FCSTD DOCUMENT  (FreeCAD 2024.2R37179 (Git))
Label: Assembly
License: All rights reserved
LicenseURL: https://en.wikipedia.org/wiki/All_rights_reserved
objects: App::Link×2, Assembly::JointGroup×1, Assembly::AssemblyObject×1
EXTERNAL_REF file=Base.FCStd obj=Body
EXTERNAL_REF file=22mm.FCStd obj=Body

FEATURE [Assembly::JointGroup] Joints
FEATURE [App::Link] Body
  LinkPlacement = pos=(38.752,-106.986,43.991) rot=(0,0,1;0rad)
  LinkedObject = -> <external Base.FCStd>#Body
  Placement = pos=(38.752,-106.986,43.991) rot=(0,0,1;0rad)
FEATURE [App::Link] Body001
  LinkPlacement = pos=(28.252,-67.4863,52.991) rot=(0,0,1;1.5708rad)
  LinkedObject = -> <external 22mm.FCStd>#Body
  Placement = pos=(28.252,-67.4863,52.991) rot=(0,0,1;1.5708rad)
FEATURE [Assembly::AssemblyObject] Assembly
  Group = -> [Joints,Body,Body001]
  Origin = -> Origin
  Type = Assembly

RESOLVED EXTERNAL PARTS (link-assembly join: the EXTERNAL_REF files above that resolve inside this repo's crawl, each included once):
---- part 22mm.FCStd = doc fcstd_51c7ecd0057d ----
FCSTD DOCUMENT  (FreeCAD 2024.2R37179 (Git))
Label: 22mm
License: All rights reserved
LicenseURL: https://en.wikipedia.org/wiki/All_rights_reserved
objects: Sketcher::SketchObject×1, PartDesign::Pad×1, PartDesign::Fillet×1, PartDesign::Body×1
note: 6 computed .brp shape members not serialized (recipe doc carries the construction recipe); baked Part::Feature solids carry a one-line shape summary decoded from their .brp

FEATURE [Sketcher::SketchObject] Sketch
  AttachmentSupport = -> [XZ_Plane]
  FullyConstrained = true
  MapMode = 5
  Placement = pos=(0,0,0) rot=(1,0,0;1.5708rad)
  sketch-geometry (4):
    g0: LineSegment StartX=0 StartY=0 StartZ=0 EndX=0 EndY=22 EndZ=0
    g1: LineSegment StartX=0 StartY=22 StartZ=0 EndX=80 EndY=10 EndZ=0
    g2: LineSegment StartX=80 StartY=10 StartZ=0 EndX=80 EndY=0 EndZ=0
    g3: LineSegment StartX=80 StartY=0 StartZ=0 EndX=0 EndY=0 EndZ=0
  constraints (11):
    c: Coincident(g-1,g0)
    c: PointOnObject(g0,g-2)
    c: Coincident(g0,g1)
    c: Coincident(g1,g2)
    c: PointOnObject(g2,g-1)
    c: Vertical(g2)
    c: Coincident(g2,g3)
    c: Coincident(g3,g0)
    c: DistanceY(g0,g0) = 22
    c: DistanceY(g2,g2) = 10
    c: DistanceX(g3,g3) = 80
FEATURE [PartDesign::Pad] Pad
  Direction = (0,-1,2e-16)
  Length = 20
  Length2 = 10
  Placement = pos=(0,0,0) rot=(1,0,0;1.5708rad)
  Profile = -> Sketch
  ReferenceAxis = -> Sketch [N_Axis]
  Refine = true
  Suppressed = false
  Type = 0
FEATURE [PartDesign::Fillet] Fillet
  Base = -> Pad [Edge6]
  BaseFeature = -> Pad
  Placement = pos=(0,0,0) rot=(1,0,0;1.5708rad)
  Radius = 2
  Refine = true
  SupportTransform = false
  Suppressed = false
  UseAllEdges = true
FEATURE [PartDesign::Body] Body
  Group = -> [Sketch,Pad,Fillet]
  Origin = -> Origin
  Tip = -> Fillet
---- part Base.FCStd = doc fcstd_2ecf710a8f8c ----
FCSTD DOCUMENT  (FreeCAD 2024.2R37179 (Git))
Label: Base
License: All rights reserved
LicenseURL: https://en.wikipedia.org/wiki/All_rights_reserved
objects: PartDesign::Fillet×5, Sketcher::SketchObject×2, PartDesign::Pad×2, PartDesign::LinearPattern×2, PartDesign::MultiTransform×1, PartDesign::Body×1
note: 20 computed .brp shape members not serialized (recipe doc carries the construction recipe); baked Part::Feature solids carry a one-line shape summary decoded from their .brp

FEATURE [Sketcher::SketchObject] Sketch
  AttachmentSupport = -> [XY_Plane]
  FullyConstrained = true
  MapMode = 5
  sketch-geometry (10):
    g0: LineSegment StartX=-37.5 StartY=-37.5 StartZ=0 EndX=37.5 EndY=-37.5 EndZ=0
    g1: LineSegment StartX=37.5 StartY=-37.5 StartZ=0 EndX=37.5 EndY=37.5 EndZ=0
    g2: LineSegment StartX=37.5 StartY=37.5 StartZ=0 EndX=10 EndY=37.5 EndZ=0
    g3: LineSegment StartX=-37.5 StartY=37.5 StartZ=0 EndX=-37.5 EndY=-37.5 EndZ=0
    g4: GeomPoint X=0 Y=0 Z=0
    g5: LineSegment StartX=-10 StartY=117.5 StartZ=0 EndX=-10 EndY=37.5 EndZ=0
    g6: LineSegment StartX=10 StartY=37.5 StartZ=0 EndX=10 EndY=117.5 EndZ=0
    g7: LineSegment StartX=10 StartY=117.5 StartZ=0 EndX=-10 EndY=117.5 EndZ=0
    g8: GeomPoint X=0 Y=77.5 Z=0
    g9: LineSegment StartX=-10 StartY=37.5 StartZ=0 EndX=-37.5 EndY=37.5 EndZ=0
  constraints (25):
    c: Coincident(g0,g1)
    c: Coincident(g1,g2)
    c: Coincident(g9,g3)
    c: Coincident(g3,g0)
    c: Horizontal(g0)
    c: Horizontal(g2)
    c: Vertical(g1)
    c: Vertical(g3)
    c: Symmetric(g2,g0,g4)
    c: Distance(g1,g3) = 75
    c: Distance(g0,g9) = 75
    c: Coincident(g4,g-1)
    c: Coincident(g6,g7)
    c: Coincident(g7,g5)
    c: Vertical(g5)
    c: Vertical(g6)
    c: Horizontal(g7)
    c: Symmetric(g6,g5,g8)
    c: PointOnObject(g8,g-2)
    c: Distance(g7,g7) = 20
    c: DistanceY(g6,g6) = 80
    c: Horizontal(g9)
    c: Coincident(g5,g9)
    c: Coincident(g6,g2)
    c: Horizontal(g5,g2)
FEATURE [PartDesign::Pad] Pad
  Direction = (0,0,1)
  Length = 3
  Length2 = 10
  Profile = -> Sketch
  ReferenceAxis = -> Sketch [N_Axis]
  Refine = true
  Suppressed = false
  Type = 0
FEATURE [PartDesign::Fillet] Fillet
  Base = -> Pad [Edge5,Edge2,Edge20,Edge1]
  BaseFeature = -> Pad
  Radius = 5
  Refine = true
  SupportTransform = false
  Suppressed = false
  UseAllEdges = false
FEATURE [Sketcher::SketchObject] Sketch001
  AttachmentSupport = -> [Fillet]
  FullyConstrained = true
  MapMode = 5
  Placement = pos=(0,0,3) rot=(0,0,1;0rad)
  sketch-geometry (1):
    g0: Circle CenterX=-30 CenterY=30 CenterZ=0 NormalX=0 NormalY=0 NormalZ=1 AngleXU=0 Radius=2.5
  constraints (3):
    c: Diameter(g0) = 5
    c: DistanceX(g0,g-1) = 30
    c: DistanceY(g-1,g0) = 30
FEATURE [PartDesign::Pad] Pad001
  BaseFeature = -> Fillet
  Direction = (0,0,1)
  Length = 1.5
  Length2 = 10
  Profile = -> Sketch001
  ReferenceAxis = -> Sketch001 [N_Axis]
  Refine = true
  Suppressed = false
  Type = 0
FEATURE [PartDesign::LinearPattern] LinearPattern
  Direction = -> X_Axis
  Length = 60
  Mode = 0
  Occurrences = 5
  Offset = 15
  Refine = true
  Suppressed = false
FEATURE [PartDesign::LinearPattern] LinearPattern001
  Direction = -> Y_Axis
  Length = 60
  Mode = 0
  Occurrences = 4
  Offset = 20
  Refine = true
  Reversed = true
  Suppressed = false
FEATURE [PartDesign::MultiTransform] MultiTransform
  BaseFeature = -> Pad001
  Originals = -> [Pad001]
  Refine = true
  Suppressed = false
  Transformations = -> [LinearPattern,LinearPattern001]
FEATURE [PartDesign::Fillet] Fillet001
  Base = -> MultiTransform [Edge4]
  BaseFeature = -> MultiTransform
  Radius = 1
  Refine = true
  SupportTransform = false
  Suppressed = false
  UseAllEdges = false
FEATURE [PartDesign::Fillet] Fillet002
  Base = -> Fillet001 [Edge32]
  BaseFeature = -> Fillet001
  Radius = 1
  Refine = true
  SupportTransform = false
  Suppressed = false
  UseAllEdges = false
FEATURE [PartDesign::Fillet] Fillet003
  Base = -> Fillet002 [Edge2,Edge1,Edge36]
  BaseFeature = -> Fillet002
  Radius = 1
  Refine = true
  SupportTransform = false
  Suppressed = false
  UseAllEdges = false
FEATURE [PartDesign::Fillet] Fillet004
  Base = -> Fillet003 [Edge104,Edge103,Edge108,Edge112,Edge116,Edge118,Edge122,Edge125,Edge123,Edge119,Edge114,Edge109,Edge126]
  BaseFeature = -> Fillet003
  Radius = 1
  Refine = true
  SupportTransform = false
  Suppressed = false
  UseAllEdges = false
FEATURE [PartDesign::Body] Body
  Group = -> [Sketch,Pad,Fillet,Sketch001,Pad001,MultiTransform,LinearPattern,LinearPattern001,Fillet001,Fillet002,Fillet003,Fillet004]
  Origin = -> Origin
  Tip = -> Fillet004
